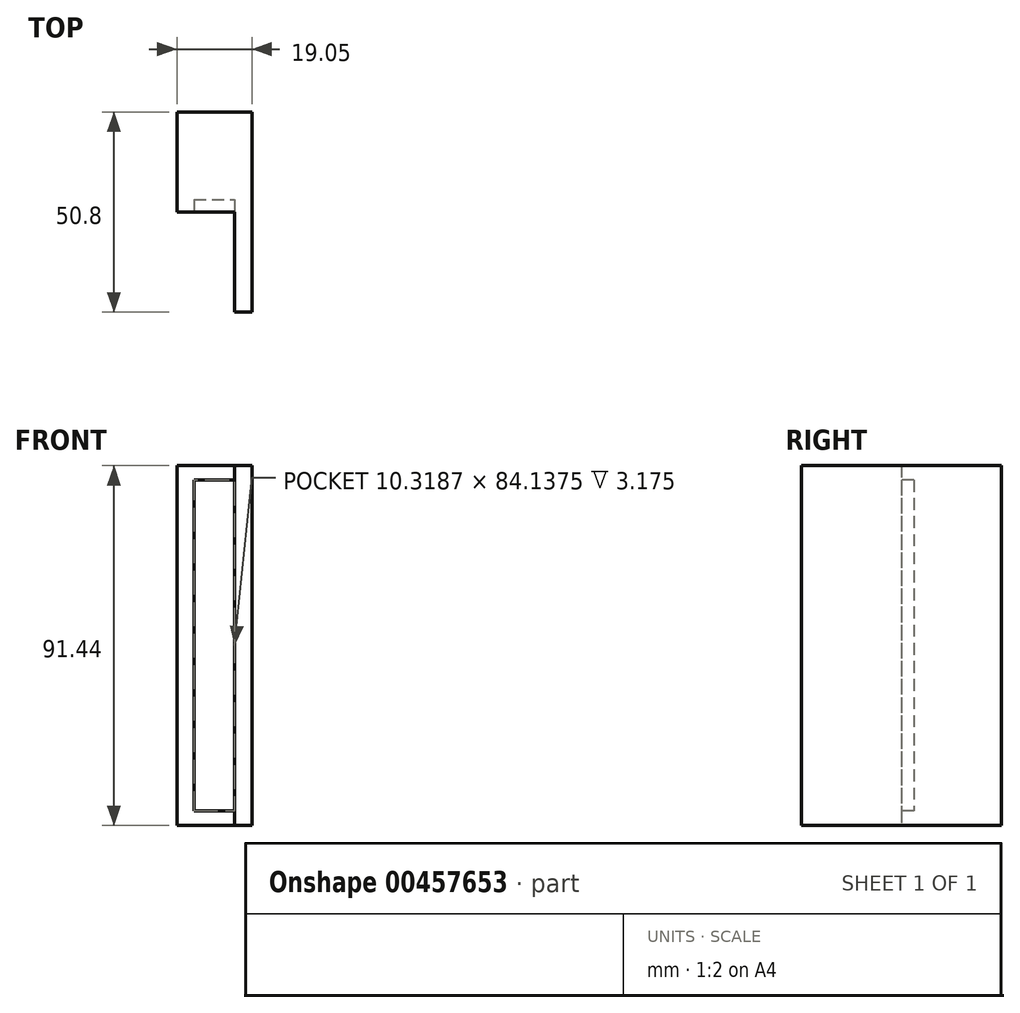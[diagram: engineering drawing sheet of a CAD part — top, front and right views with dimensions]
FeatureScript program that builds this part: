
annotation { "Feature Type Name" : "Feature", "Feature Type Description" : "" }
export const myFeature = defineFeature(function(context is Context, id is Id, definition is map)
    precondition{}
    {
        {
            var Q0;
            Q0=qCreatedBy(makeId("Front.planeOp"),FACE);
            var sketch = newSketch(context, id + "F0", { "sketchPlane" : qUnion([Q0])});
            skLineSegment(sketch, "E0.bottom", {"start": v(-61.9, 74.32) * mm, "end": v(-51.58, 74.32) * mm});
            skLineSegment(sketch, "E0.top", {"start": v(-61.9, -9.82) * mm, "end": v(-51.58, -9.82) * mm});
            skLineSegment(sketch, "E0.left", {"start": v(-61.9, 74.32) * mm, "end": v(-61.9, -9.82) * mm});
            skLineSegment(sketch, "E0.right", {"start": v(-51.58, 74.32) * mm, "end": v(-51.58, -9.82) * mm});
            skSolve(sketch);
        }
        {
            var Q0;
            Q0=makeQuery(id+"F0.imprint","IMPRINT",FACE,{"disambiguationData":[TD([[makeQuery(id+"F0.imprint","IMPRINT",EDGE,{"derivedFrom":sQuery(id+"F0.wireOp",EDGE,"E0.bottom")}),-1.0]])]});
            extrude(context, id + "F1", {"entities" : qUnion([Q0]), "depth" : 1.59 * mm});
        }
        {
            var Q0;
            Q0=makeQuery(id+"F1.opExtrude","CAP_FACE",FACE,{"disambiguationData":[OSD([sQuery(id+"F0.wireOp",EDGE,"E0.bottom"),sQuery(id+"F0.wireOp",EDGE,"E0.top"),sQuery(id+"F0.wireOp",EDGE,"E0.left"),sQuery(id+"F0.wireOp",EDGE,"E0.right")])],"isStart":true});
            var sketch = newSketch(context, id + "F2", { "sketchPlane" : qUnion([Q0])});
            skLineSegment(sketch, "E1.bottom", {"start": v(47.21, 77.97) * mm, "end": v(66.26, 77.97) * mm});
            skLineSegment(sketch, "E1.top", {"start": v(47.21, -13.47) * mm, "end": v(66.26, -13.47) * mm});
            skLineSegment(sketch, "E1.left", {"start": v(47.21, 77.97) * mm, "end": v(47.21, -13.47) * mm});
            skLineSegment(sketch, "E1.right", {"start": v(66.26, 77.97) * mm, "end": v(66.26, -13.47) * mm});
            skPoint(sketch, "E1.middle", {"position": v(56.74, 32.25) * mm});
            skPoint(sketch, "E1.middle.positionSnap0", {"position": v(56.74, 74.32) * mm});
            skPoint(sketch, "E1.middle.positionSnap1", {"position": v(51.58, 32.25) * mm});
            skPoint(sketch, "E1.centerSnap0", {"position": v(56.74, 74.32) * mm});
            skPoint(sketch, "E1.centerSnap1", {"position": v(51.58, 32.25) * mm});
            skSolve(sketch);
        }
        {
            var Q0;
            Q0 = qSketchRegion(id + "F2", true);
            extrude(context, id + "F3", {"entities" : qUnion([Q0]), "operationType" : NewBodyOperationType.ADD, "depth" : 25.4 * mm});
        }
        {
            var Q0;
            Q0=makeQuery(id+"F1.opExtrude","CAP_FACE",FACE,{"disambiguationData":[OSD([sQuery(id+"F0.wireOp",EDGE,"E0.bottom"),sQuery(id+"F0.wireOp",EDGE,"E0.top"),sQuery(id+"F0.wireOp",EDGE,"E0.left"),sQuery(id+"F0.wireOp",EDGE,"E0.right")])],"isStart":false});
            var sketch = newSketch(context, id + "F4", { "sketchPlane" : qUnion([Q0])});
            skLineSegment(sketch, "E2.bottom", {"start": v(-61.9, 74.32) * mm, "end": v(-51.58, 74.32) * mm});
            skLineSegment(sketch, "E2.top", {"start": v(-61.9, -9.82) * mm, "end": v(-51.58, -9.82) * mm});
            skLineSegment(sketch, "E2.left", {"start": v(-61.9, 74.32) * mm, "end": v(-61.9, -9.82) * mm});
            skLineSegment(sketch, "E2.right", {"start": v(-51.58, 74.32) * mm, "end": v(-51.58, -9.82) * mm});
            skSolve(sketch);
        }
        {
            var Q0;
            Q0 = qSketchRegion(id + "F4", true);
            extrude(context, id + "F5", {"entities" : qUnion([Q0]), "operationType" : NewBodyOperationType.REMOVE, "oppositeDirection" : true, "depth" : 4.76 * mm});
        }
        {
            var Q0;
            Q0=makeQuery(id+"F3.opExtrude","CAP_FACE",FACE,{"disambiguationData":[OSD([sQuery(id+"F2.wireOp",EDGE,"E1.bottom"),sQuery(id+"F2.wireOp",EDGE,"E1.top"),sQuery(id+"F2.wireOp",EDGE,"E1.left"),sQuery(id+"F2.wireOp",EDGE,"E1.right")])],"isStart":true});
            var sketch = newSketch(context, id + "F6", { "sketchPlane" : qUnion([Q0])});
            skLineSegment(sketch, "E3.bottom", {"start": v(-47.21, 77.97) * mm, "end": v(-51.58, 77.97) * mm});
            skLineSegment(sketch, "E3.top", {"start": v(-47.21, -13.47) * mm, "end": v(-51.58, -13.47) * mm});
            skLineSegment(sketch, "E3.left", {"start": v(-47.21, 77.97) * mm, "end": v(-47.21, -13.47) * mm});
            skLineSegment(sketch, "E3.right", {"start": v(-51.58, 77.97) * mm, "end": v(-51.58, -13.47) * mm});
            skSolve(sketch);
        }
        {
            var Q0;
            Q0 = qSketchRegion(id + "F6", true);
            extrude(context, id + "F7", {"entities" : qUnion([Q0]), "operationType" : NewBodyOperationType.ADD, "depth" : 25.4 * mm});
        }
    });
